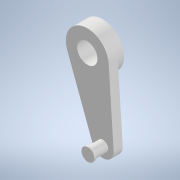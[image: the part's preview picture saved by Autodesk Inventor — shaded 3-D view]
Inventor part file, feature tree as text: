
AUTODESK INVENTOR PART (.ipt)
format: ipt  version: 2022 (Build 260153000, 153)  size: 175,104 bytes
history: native  units: mm
features: other x8, extrude x4, sketch x4, fillet x3, reference x3, projected_geometry x2
ambient origin geometry x8: Origin, YZ Plane, XZ Plane, XY Plane, X Axis, Y Axis, Z Axis, Center Point
bodies: Body1 (feature_tree)
feature tree (24):
  other  "Твердое тело1"
  extrude  "Выдавливание1"  Depth=2.2mm
  extrude  "Выдавливание2"  Depth=4.0mm
  fillet  "Сопряжение1"  Radius=8.0mm
  extrude  "Выдавливание3"  Depth=1.7mm TaperAngle=0.0deg
  extrude  "Выдавливание4"  Depth=3.8mm
  fillet  "Сопряжение2"  Radius=1.2mm
  fillet  "Сопряжение3"  Radius=0.5mm
  sketch  "Эскиз1"
  reference  "Ссылка1"
  reference  "Ссылка2"
  sketch  "Эскиз2"
  projected_geometry  "Спроецированная петля1"
  sketch  "Эскиз3"
  reference  "Ссылка3"
  sketch  "Эскиз4"
  projected_geometry  "Спроецированная петля2"
  other  "<userpath>\Documents\Git\MZCAT_2024\MZCAT_2.iam"
  other  "MZCAT_2.iam"
  other  "OCS-D008 B:2"
  other  "lidar_krestovina:1"
  other  "<userpath>\Documents\Git\MZCAT_2024\MZCAT_3.iam"
  other  "MZCAT_3.iam"
  other  "lidar_shatun_main2:1"
